# Revit family: PRD_FrankeWS_WlMntdBbTps_OutletExtension_AQRM909
name_source: partatom
category: Specialty Equipment
revit_build: Autodesk Revit 2018 (Build: 20190510_1515(x64)
units: mm (PartAtom-declared; Revit-internal decimal feet)

## family parameters
Always vertical = No
Cut with Voids When Loaded = No
OmniClass Number = 23.45.55.11
OmniClass Title = Sanitary Components
Part Type = Normal
Room Calculation Point = No
Round Connector Dimension = Use Diameter
Shared = No
Work Plane-Based = Yes

## types (1)
- AQRM909
    AssetType = Fixed
    BIMObjectName = PRD_AR_WallMountedBibTaps_OutletExtension_AQRM909
    BodyMaterial = PRD_AR_ChromatedBrass_HighPolished
    Category = Pr_40_20_87_93, Wall-mounted bib taps
    Color = Chrome
    Default Elevation = 1219 mm
    Description = Spout extension M 24 x 1, stackable, for taps, length 30 mm, polished chromium-plated brass.
    DurationUnit = year
    Features = polished chromium-plated brass
    Finish = polished chromium-plated
    GrossWeight = 0.14 kg
    IfcExportAs = IfcValveType
    IfcExportType = FAUCET
    Manufacturer = KWC Group AG
    ManufacturerName = KWC Group AG
    ManufacturerURL = www.kwc.com
    Material = Brass
    Model = AQRM909
    ModelNumber = 2000101463
    ModelReference = AQRM909
    NBSDescription = Taps and water supply fittings for sinks
    NBSReference = 45-35-70/345
    Name = Outlet extension AQRM909
    NetWeight = 0.14 kg
    NominalDepth = 30 mm  [stored 0.0984252 ft]
    NominalHeight = 30 mm  [stored 0.0984252 ft]
    NominalWidth = 30 mm  [stored 0.0984252 ft]
    ProductCode = 208.0637.678
    ProductInformation = https://pim.kwc.com
    TypeOfExtension = Spout extension
    URL = www.kwc.com
    Uniclass2015Code = Pr_40_20_87_93
    Uniclass2015Title = Wall-mounted bib taps
    Uniclass2015Version = Products v1.23
    Version = 1
    WarrantyDurationUnit = year

note: [stored X ft] marks values corroborated as IEEE doubles in the binary element streams (Revit-internal decimal feet)

## geometry (parser evidence)
native form markers: Sweep x3
no freeform markers — native parametric forms only
